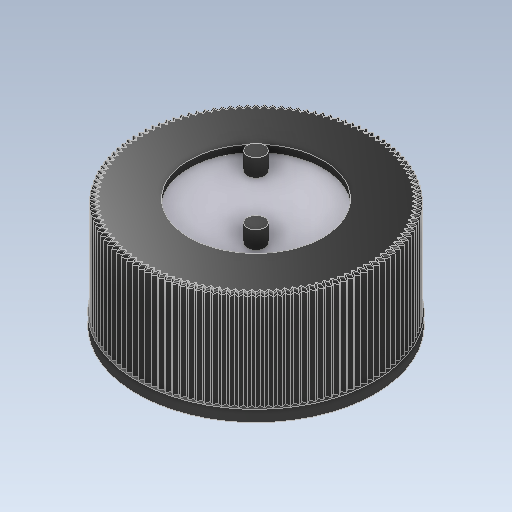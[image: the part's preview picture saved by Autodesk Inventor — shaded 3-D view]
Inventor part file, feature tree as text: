
AUTODESK INVENTOR PART (.ipt)
format: ipt  version: 2021 (Build 250183000, 183)  size: 921,600 bytes
history: native  units: mm
features: sketch x5, extrude x4, fillet x1
ambient origin geometry x8: Origin, YZ Plane, XZ Plane, XY Plane, X Axis, Y Axis, Z Axis, Center Point
bodies: Solid1 (feature_tree)
feature tree (10):
  extrude  "Extrusion1"  Depth=1.3mm TaperAngle=0.0deg
  extrude  "Extrusion2"  Depth=25.6mm
  sketch  "Sketch3"  dims[d9=11.0mm d10=0.0mm d11=0.25mm]
  fillet  "Fillet1"  Radius=1200.0mm
  extrude  "Extrusion3"  Depth=0.25mm
  extrude  "Extrusion4"  Depth=0.8mm TaperAngle=0.0deg
  sketch  "Sketch1"  dims[d0=26.7mm d1=1.3mm d2=0.0mm]
  sketch  "Sketch2"  dims[d3=26.4mm d4=25.6mm d5=1200.0mm d7=360.0deg]
  sketch  "Sketch4"  dims[d12=15.0mm d13=0.8mm d14=0.0mm]
  sketch  "Sketch5"  dims[d15=2.0mm d16=2.0mm d17=7.0mm d18=7.0mm d19=2.0mm d20=0.0mm]
